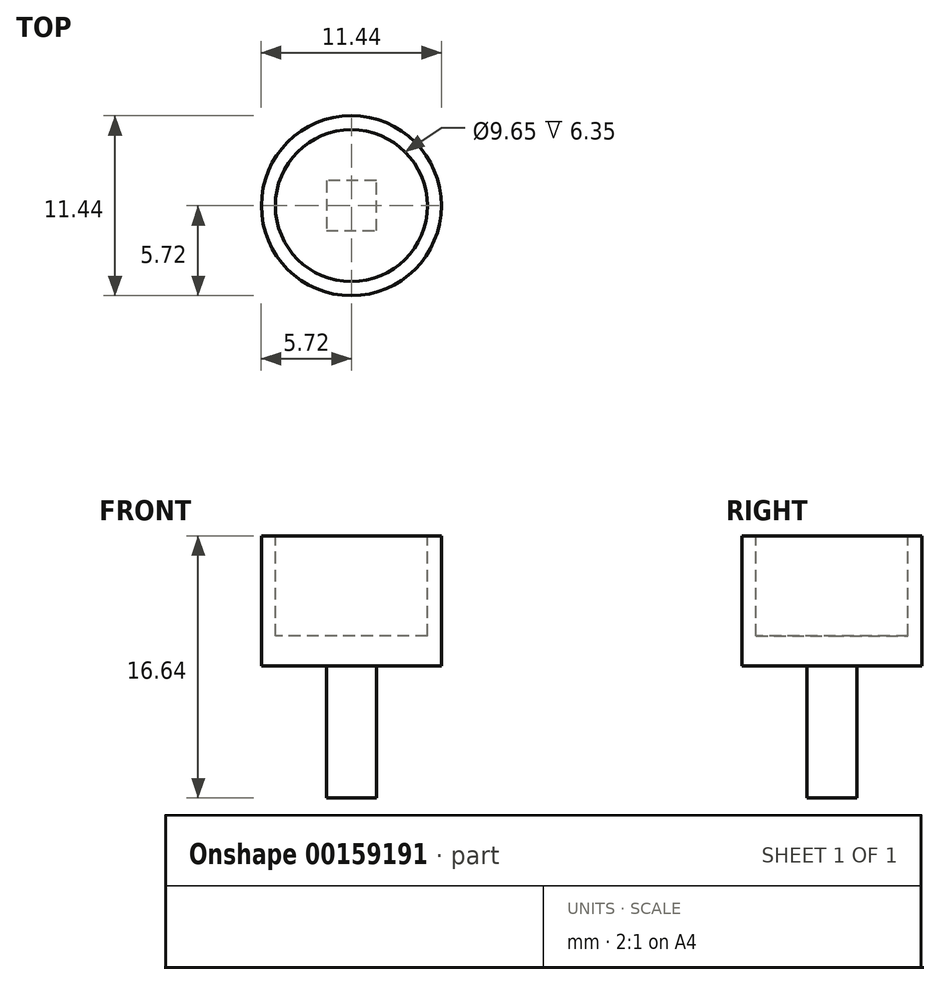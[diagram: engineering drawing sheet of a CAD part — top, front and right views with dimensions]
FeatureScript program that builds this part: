
annotation { "Feature Type Name" : "Feature", "Feature Type Description" : "" }
export const myFeature = defineFeature(function(context is Context, id is Id, definition is map)
    precondition{}
    {
        {
            var Q0;
            Q0=qCreatedBy(makeId("Top.planeOp"),FACE);
            var sketch = newSketch(context, id + "F0", { "sketchPlane" : qUnion([Q0])});
            skLineSegment(sketch, "E0", {"start": v(0, 0) * mm, "end": v(1.59, 0) * mm});
            skLineSegment(sketch, "E1", {"start": v(1.59, 0) * mm, "end": v(1.59, 1.59) * mm});
            skLineSegment(sketch, "E2", {"start": v(1.59, 1.59) * mm, "end": v(-1.59, 1.59) * mm});
            skLineSegment(sketch, "E3", {"start": v(-1.59, 1.59) * mm, "end": v(-1.59, -1.59) * mm});
            skLineSegment(sketch, "E4", {"start": v(-1.59, -1.59) * mm, "end": v(1.59, -1.59) * mm});
            skLineSegment(sketch, "E5", {"start": v(1.59, -1.59) * mm, "end": v(1.59, 0) * mm});
            skSolve(sketch);
        }
        {
            var Q0;
            Q0 = qSketchRegion(id + "F0", true);
            extrude(context, id + "F1", {"entities" : qUnion([Q0]), "depth" : 8.38 * mm});
        }
        {
            var Q0;
            Q0=makeQuery(id+"F1.opExtrude","CAP_FACE",FACE,{"disambiguationData":[OSD([sQuery(id+"F0.wireOp",EDGE,"E1"),sQuery(id+"F0.wireOp",EDGE,"E2"),sQuery(id+"F0.wireOp",EDGE,"E3"),sQuery(id+"F0.wireOp",EDGE,"E4"),sQuery(id+"F0.wireOp",EDGE,"E5")])],"isStart":false});
            var sketch = newSketch(context, id + "F2", { "sketchPlane" : qUnion([Q0])});
            skCircle(sketch, "E6", {"center": v(0, 0) * mm, "radius": 5.72 * mm});
            skSolve(sketch);
        }
        {
            var Q0;
            Q0 = qSketchRegion(id + "F2", true);
            extrude(context, id + "F3", {"entities" : qUnion([Q0]), "operationType" : NewBodyOperationType.ADD, "depth" : 8.25 * mm});
        }
        {
            var Q0;
            Q0=makeQuery(id+"F3.opExtrude","CAP_FACE",FACE,{"disambiguationData":[OSD([sQuery(id+"F2.wireOp",EDGE,"E6")])],"isStart":false});
            var sketch = newSketch(context, id + "F4", { "sketchPlane" : qUnion([Q0])});
            skCircle(sketch, "E7", {"center": v(0, 0) * mm, "radius": 4.83 * mm});
            skSolve(sketch);
        }
        {
            var Q0;
            Q0 = qSketchRegion(id + "F4", true);
            extrude(context, id + "F5", {"entities" : qUnion([Q0]), "operationType" : NewBodyOperationType.REMOVE, "oppositeDirection" : true, "depth" : 6.35 * mm});
        }
    });
